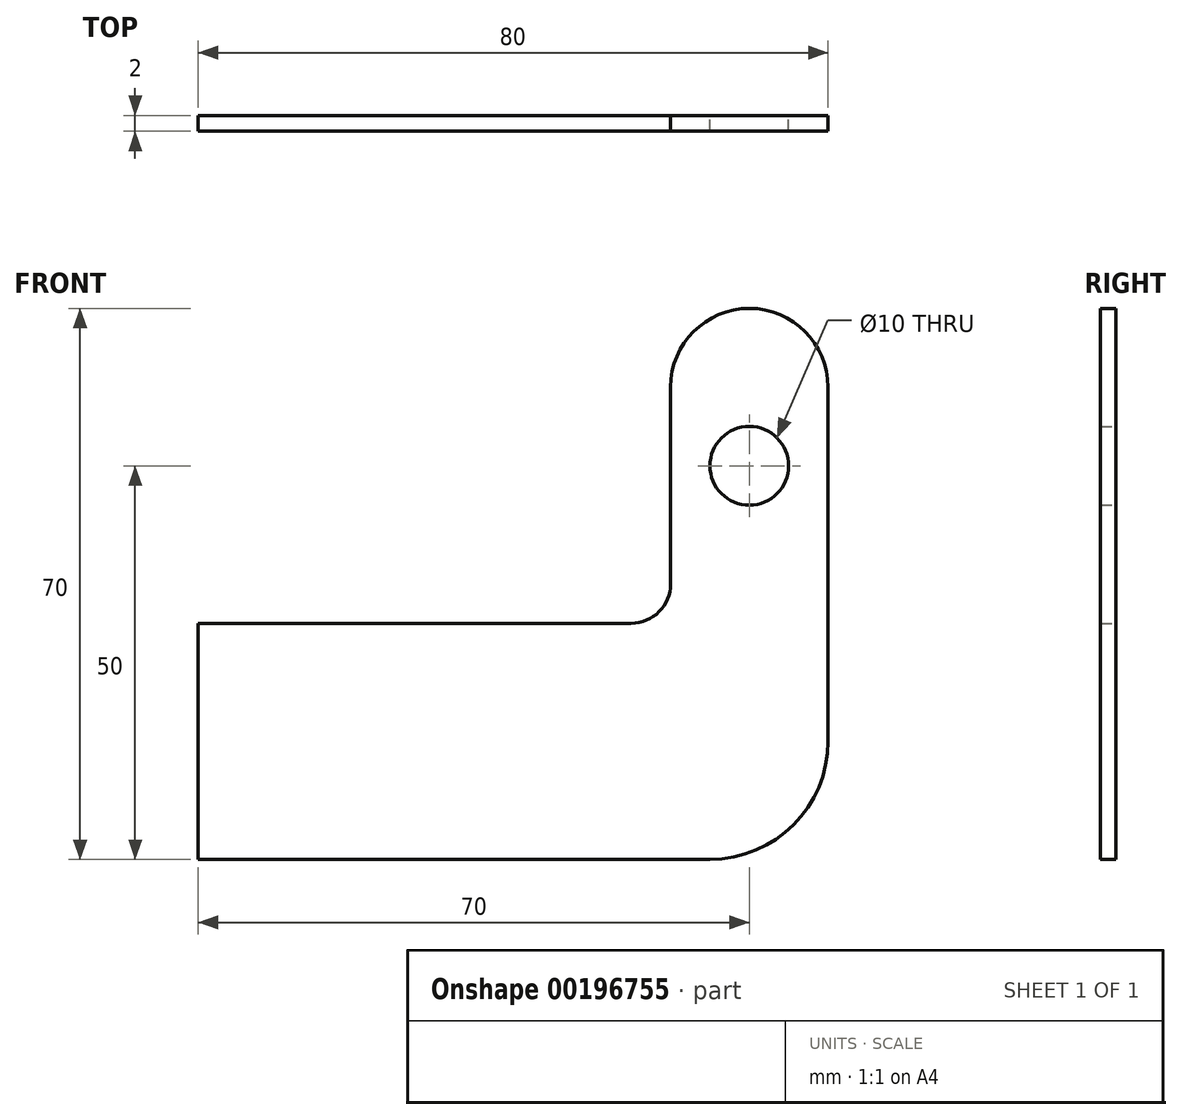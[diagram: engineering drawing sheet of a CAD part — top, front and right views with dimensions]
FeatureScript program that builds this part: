
annotation { "Feature Type Name" : "Feature", "Feature Type Description" : "" }
export const myFeature = defineFeature(function(context is Context, id is Id, definition is map)
    precondition{}
    {
        {
            var Q0;
            Q0=qCreatedBy(makeId("Front.planeOp"),FACE);
            var sketch = newSketch(context, id + "F0", { "sketchPlane" : qUnion([Q0])});
            skLineSegment(sketch, "E0.bottom", {"start": v(0, 0) * mm, "end": v(65, 0) * mm});
            skLineSegment(sketch, "E0.top", {"start": v(70, 70) * mm, "end": v(70, 70) * mm});
            skLineSegment(sketch, "E0.right", {"start": v(80, 15) * mm, "end": v(80, 60) * mm});
            skLineSegment(sketch, "E1", {"start": v(0, 0) * mm, "end": v(70, 0) * mm});
            skCircle(sketch, "E2", {"center": v(70, 50) * mm, "radius": 5 * mm});
            skLineSegment(sketch, "E3", {"start": v(0, 0) * mm, "end": v(0, 30) * mm});
            skLineSegment(sketch, "E4", {"start": v(0, 30) * mm, "end": v(55, 30) * mm});
            skLineSegment(sketch, "E5", {"start": v(60, 35) * mm, "end": v(60, 60) * mm});
            skPoint(sketch, "E6.visualSharp", {"position": v(60, 30) * mm});
            skArc(sketch, "E6.filletArc", {"start": v(55, 30) * mm, "mid": v(58.54, 31.46) * mm, "end": v(60, 35) * mm});
            skPoint(sketch, "E7.visualSharp", {"position": v(80, 0) * mm});
            skArc(sketch, "E7.filletArc", {"start": v(65, 0) * mm, "mid": v(75.6, 4.4) * mm, "end": v(80, 15) * mm});
            skPoint(sketch, "E8.visualSharp", {"position": v(80, 70) * mm});
            skArc(sketch, "E8.filletArc", {"start": v(80, 60) * mm, "mid": v(77.07, 67.07) * mm, "end": v(70, 70) * mm});
            skArc(sketch, "E9.filletArc", {"start": v(70, 70) * mm, "mid": v(62.93, 67.07) * mm, "end": v(60, 60) * mm});
            skSolve(sketch);
        }
        {
            var Q0;
            Q0 = qSketchRegion(id + "F0", true);
            extrude(context, id + "F1", {"entities" : qUnion([Q0]), "depth" : 2 * mm});
        }
    });
